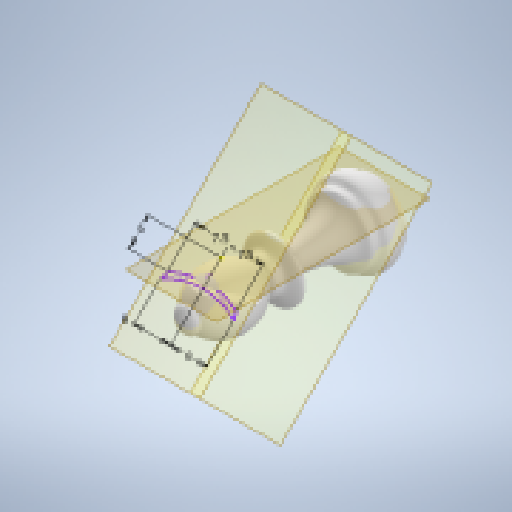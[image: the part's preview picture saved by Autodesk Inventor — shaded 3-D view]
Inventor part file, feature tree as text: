
AUTODESK INVENTOR PART (.ipt)
format: ipt  version: 2024.1 (Build 281209000, 209)  size: 451,584 bytes
history: native  units: mm
features: sketch x5, plane x3, extrude x2, other x1, revolve x1, fillet x1, sweep x1, projected_geometry x1
ambient origin geometry x8: Origin, YZ Plane, XZ Plane, XY Plane, X Axis, Y Axis, Z Axis, Center Point
bodies: Solid1 (feature_tree)
feature tree (15):
  extrude  "Extrusion1"  Depth=3.0mm TaperAngle=0.0deg
  other  "Work Axis1"
  extrude  "Extrusion2"  Depth=14.3mm
  revolve  "Revolution1"  [1 undecoded]
  fillet  "Fillet5"  Radius=0.6mm
  plane  "Work Plane6"
  plane  "Work Plane9"
  sweep  "Sweep1"
  sketch  "Sketch1"  dims[d0=10.0mm d1=3.0mm d2=0.0mm]
  sketch  "Sketch2"  dims[d5=360.0deg d6=14.3mm]
  sketch  "Sketch3"  dims[d7=3.0mm d8=0.0mm d89=12.3mm d107=0.6mm]
  projected_geometry  "Projected Loop1"
  plane  "Work Plane7"
  sketch  "Sketch16"  dims[d127=2.8mm d128=1.4mm]
  sketch  "Sketch17"  dims[d129=6.3mm d130=8.0mm d131=8.0mm d132=33.0mm d133=11.2mm d134=6.75mm d135=0.8mm d136=25.0mm d137=8.0mm d138=8.0mm d141=6.0mm d142=7.5mm d143=7.5mm d144=0.0mm d145=0.0mm d98=0.0mm d99=0.0mm d100=0.0mm d101=0.0mm]
note: 1 required parameter value undecoded (feature->parameter linkage not recoverable at this tier; creation-order binding heuristic only, values carry confidence <= 0.55)
